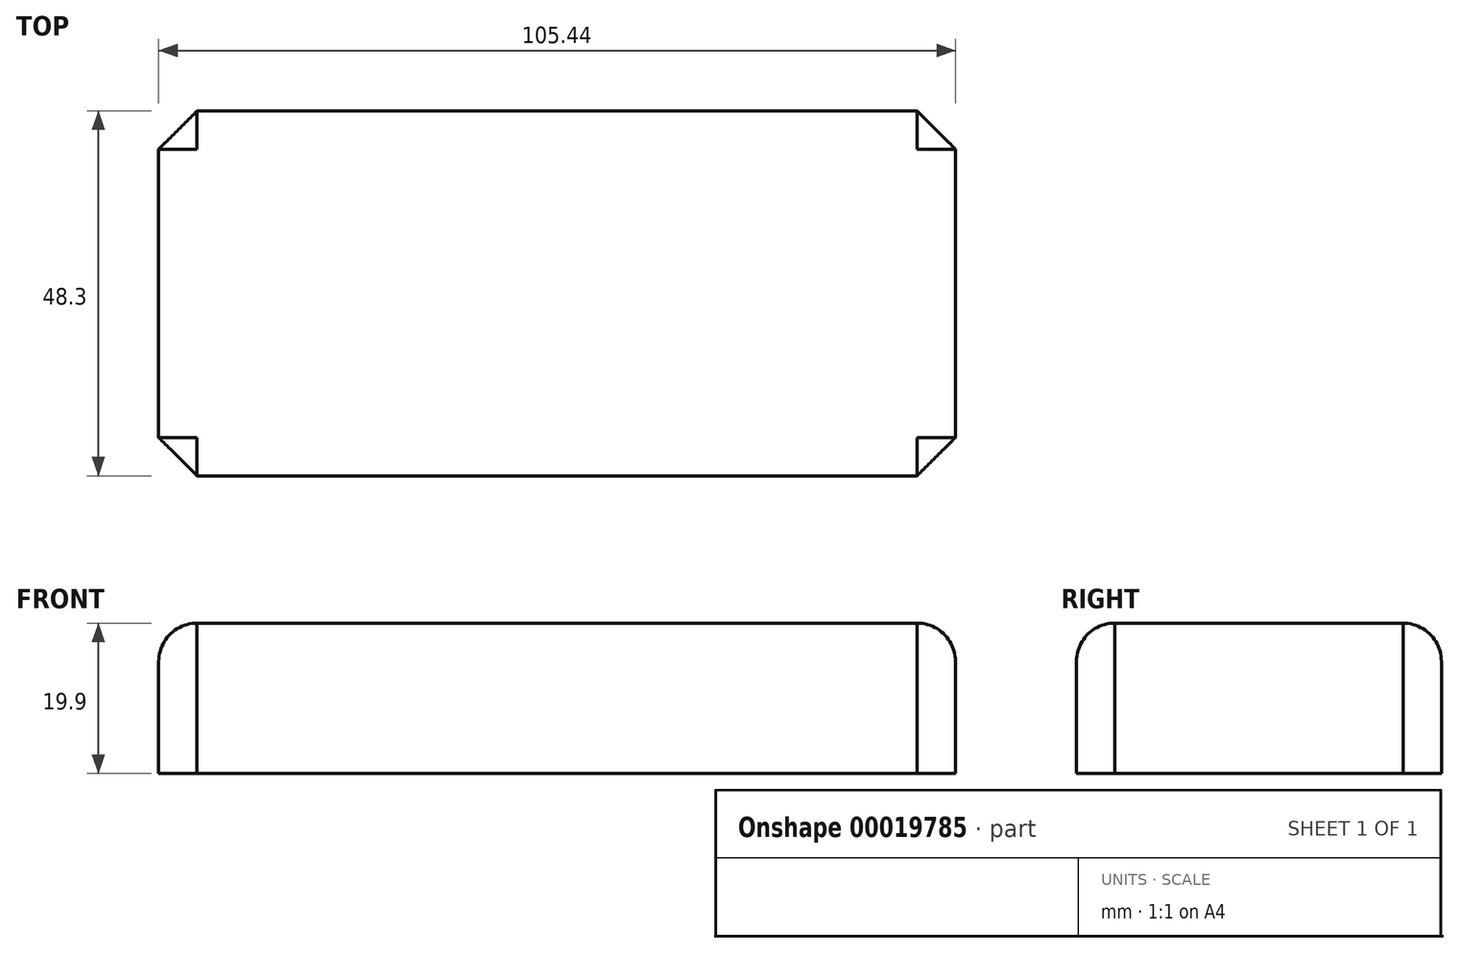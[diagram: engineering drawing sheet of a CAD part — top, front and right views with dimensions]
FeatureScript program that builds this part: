
annotation { "Feature Type Name" : "Feature", "Feature Type Description" : "" }
export const myFeature = defineFeature(function(context is Context, id is Id, definition is map)
    precondition{}
    {
        {
            var Q0;
            Q0=qCreatedBy(makeId("Top.planeOp"),FACE);
            var sketch = newSketch(context, id + "F0", { "sketchPlane" : qUnion([Q0])});
            skLineSegment(sketch, "E0.rect.bottom", {"start": v(52.72, -24.15) * mm, "end": v(-52.72, -24.15) * mm});
            skLineSegment(sketch, "E0.rect.top", {"start": v(52.72, 24.15) * mm, "end": v(-52.72, 24.15) * mm});
            skLineSegment(sketch, "E0.rect.left", {"start": v(52.72, -24.15) * mm, "end": v(52.72, 24.15) * mm});
            skLineSegment(sketch, "E0.rect.right", {"start": v(-52.72, -24.15) * mm, "end": v(-52.72, 24.15) * mm});
            skPoint(sketch, "E0.rect.middle", {"position": v(0, 0) * mm});
            skSolve(sketch);
        }
        {
            var Q0;
            Q0=makeQuery(id+"F0.imprint","IMPRINT",FACE,{"disambiguationData":[TD([[makeQuery(id+"F0.imprint","IMPRINT",EDGE,{"derivedFrom":sQuery(id+"F0.wireOp",EDGE,"E0.rect.bottom")}),-1.0]])]});
            extrude(context, id + "F1", {"entities" : qUnion([Q0]), "depth" : 19.9 * mm});
        }
        {
            var Q0;
            Q0=makeQuery(id+"F1.opExtrude","CAP_EDGE",EDGE,{"disambiguationData":[OSD([sQuery(id+"F0.wireOp",EDGE,"E0.rect.bottom")])],"isStart":false});
            var Q1;
            Q1=makeQuery(id+"F1.opExtrude","CAP_EDGE",EDGE,{"disambiguationData":[OSD([sQuery(id+"F0.wireOp",EDGE,"E0.rect.right")])],"isStart":false});
            var Q2;
            Q2=makeQuery(id+"F1.opExtrude","CAP_EDGE",EDGE,{"disambiguationData":[OSD([sQuery(id+"F0.wireOp",EDGE,"E0.rect.top")])],"isStart":false});
            var Q3;
            Q3=makeQuery(id+"F1.opExtrude","CAP_EDGE",EDGE,{"disambiguationData":[OSD([sQuery(id+"F0.wireOp",EDGE,"E0.rect.left")])],"isStart":false});
            fillet(context, id + "F2", {"entities" : qUnion([Q0, Q1, Q2, Q3]), "radius" : 5.08 * mm, "tangentPropagation" : true, "allowEdgeOverflow" : false});
        }
        {
            var Q0;
            Q0=makeQuery(id+"F1.opExtrude","SWEPT_EDGE",EDGE,{"disambiguationData":[OSD([sQuery(id+"F0.wireOp",EDGE,"E0.rect.bottom"),sQuery(id+"F0.wireOp",EDGE,"E0.rect.right")])]});
            var Q1;
            Q1=makeQuery(id+"F1.opExtrude","SWEPT_EDGE",EDGE,{"disambiguationData":[OSD([sQuery(id+"F0.wireOp",EDGE,"E0.rect.bottom"),sQuery(id+"F0.wireOp",EDGE,"E0.rect.left")])]});
            var Q2;
            Q2=makeQuery(id+"F1.opExtrude","SWEPT_EDGE",EDGE,{"disambiguationData":[OSD([sQuery(id+"F0.wireOp",EDGE,"E0.rect.top"),sQuery(id+"F0.wireOp",EDGE,"E0.rect.left")])]});
            var Q3;
            Q3=makeQuery(id+"F1.opExtrude","SWEPT_EDGE",EDGE,{"disambiguationData":[OSD([sQuery(id+"F0.wireOp",EDGE,"E0.rect.top"),sQuery(id+"F0.wireOp",EDGE,"E0.rect.right")])]});
            chamfer(context, id + "F3", {"entities" : qUnion([Q0, Q1, Q2, Q3]), "width" : 5.08 * mm, "tangentPropagation" : true});
        }
    });
